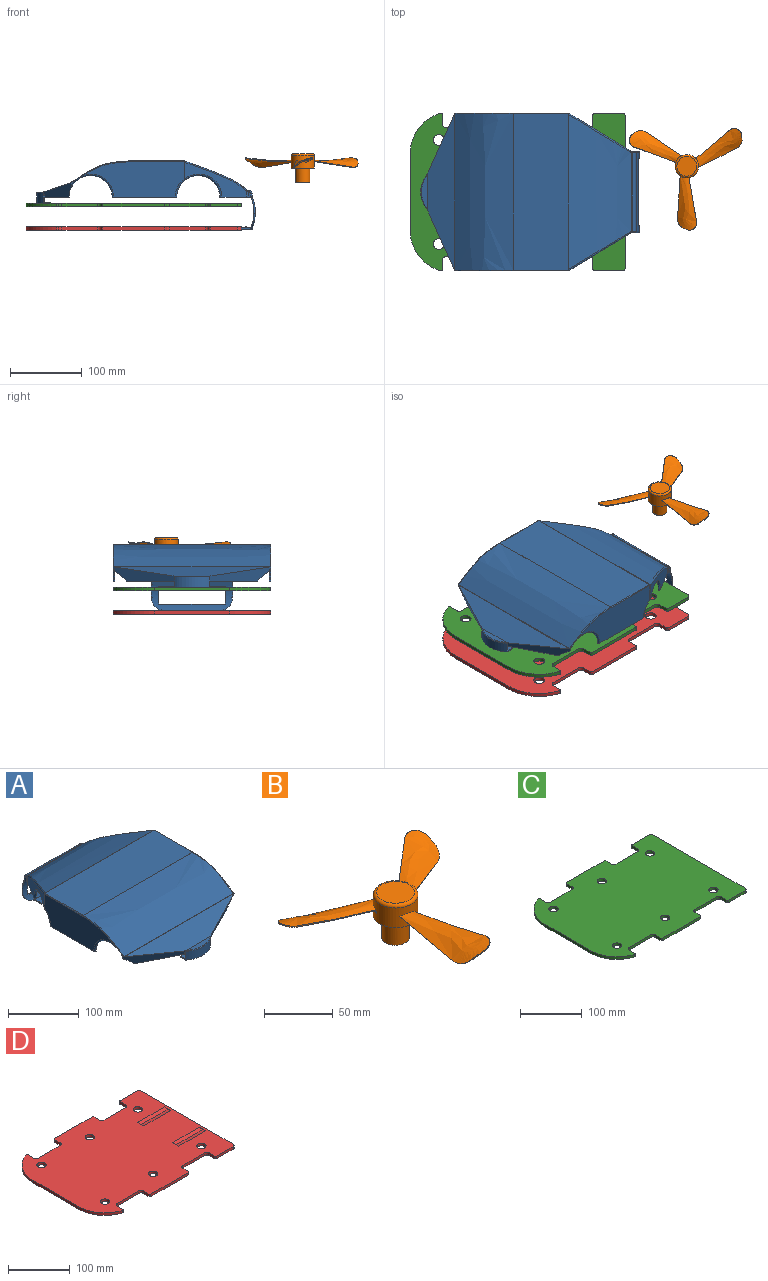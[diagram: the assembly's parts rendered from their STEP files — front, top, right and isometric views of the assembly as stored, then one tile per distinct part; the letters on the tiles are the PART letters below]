
ASSEMBLY  parts=4 mates=1
PART A: 142 faces, bbox 290.9x334.2x135.4 mm
  f0: plane 140.21x49.36mm, normal (-1,0,0), area 5203mm2, adj f11,f53,f54,f100,f103,f104,f107
  f1: plane 4.65x4.5mm, normal (1,0,0), area 5.3mm2, adj f18,f25,f92,f108
  f2: plane 69.31x35.81mm, normal (0,0,-1), area 196.7mm2, adj f10,f24,f26,f47,f49,f63
  f3: plane 69.31x35.81mm, normal (0,0,-1), area 196.7mm2, adj f10,f25,f27,f48,f50,f62
  f4: plane 7.65x3.42mm, normal (1,0,0), area 22.2mm2, adj f6,f8,f82,f131,f132,f133,f134
  f5: plane 7.65x3.42mm, normal (-1,0,0), area 22.2mm2, adj f6,f8,f83,f116,f117,f118,f119
  f6: cylinder r=51mm len=113mm, axis (1,0,0), area 2556.2mm2, adj f4,f5,f8,f56,f57,f58,f59,f60
  f7: cylinder r=51mm len=109.01mm, axis (1,0,0), area 2172.4mm2, adj f58,f59,f60,f61,f76,f84,f111,f112
  f8: plane 156.92x43.12mm, normal (0,0,-1), area 296.3mm2, adj f4,f5,f6,f28,f29,f30,f31,f32
  f9: cylinder r=30mm len=44.38mm, axis (1,0,0), area 38.2mm2, adj f11,f31,f35,f100,f101
  f10: cylinder r=30mm len=216mm, axis (1,0,0), area 2858.4mm2, adj f2,f3,f11,f20,f24,f25,f35,f36
  f11: plane 90x2.5mm, normal (0,0,-1), area 223.3mm2, adj f0,f9,f10,f35,f100,f107
  f12: plane 109x3.29mm, normal (0,1,0), area 358.1mm2, adj f84,f85,f117,f133
  f13: plane 109.15x1.32mm, normal (0,0,1), area 143.8mm2, adj f52,f85,f119,f120,f130,f131
  f14: extruded ~215.73x86.9mm, area 15564.6mm2, adj f52,f122,f123,f125,f127,f128
  f15: plane 140.2x49.35mm, normal (1,0,0), area 5203mm2, adj f20,f55,f86,f94,f96,f98,f108
  f16: plane 4.65x4.5mm, normal (-1,0,0), area 5.3mm2, adj f18,f24,f90,f107
  f17: cylinder r=30mm len=44.38mm, axis (1,0,0), area 38.2mm2, adj f20,f32,f36,f93,f94
  f18: plane 220x39.17mm, normal (0,-0.32,0.95), area 5384.8mm2, adj f1,f16,f19,f24,f25,f51,f90,f91
  f19: plane 46.85x8.19mm, normal (0,0,1), area 261.9mm2, adj f18,f51
  f20: plane 90x2.5mm, normal (0,0,-1), area 223.3mm2, adj f10,f15,f17,f36,f94,f108
  f21: plane 218x76.61mm, normal (0,0,1), area 16698.8mm2, adj f53,f86,f88,f99,f106,f125
  f22: extruded ~218x81.16mm, area 19256.8mm2, adj f54,f55,f88,f91
  f23: cylinder r=38.6mm len=50mm, axis (0,0,1), area 815.8mm2, adj f26,f27,f51,f62,f63,f65,f66,f68
  f24: plane 86.5x40.17mm, normal (-0.43,-0.86,-0.29), area 1148.9mm2, adj f2,f10,f16,f18,f26,f51,f107
  f25: plane 86.5x40.17mm, normal (0.43,-0.86,-0.29), area 1148.9mm2, adj f1,f3,f10,f18,f27,f51,f108
  f26: plane 6.55x2.41mm, normal (-1,0,0), area 8.2mm2, adj f2,f23,f24,f51
  f27: plane 6.55x2.41mm, normal (1,0,0), area 8.2mm2, adj f3,f23,f25,f51
  f28: plane 85.83x52.48mm, normal (0.85,0.52,0), area 1537mm2, adj f8,f82,f93,f96,f99,f127
  f29: plane 85.83x52.48mm, normal (-0.85,0.52,0), area 1537mm2, adj f8,f83,f101,f103,f106,f123
  f30: plane 6.86x4.89mm, normal (1,0,0), area 28.2mm2, adj f8,f31,f39,f81
  f31: plane 113.84x79.83mm, normal (0.85,-0.52,0), area 1661.3mm2, adj f8,f9,f30,f34,f35,f37,f38,f81
  f32: plane 113.84x79.83mm, normal (-0.85,-0.52,0), area 1661.3mm2, adj f8,f17,f33,f34,f36,f37,f38,f81
  f33: plane 6.86x4.89mm, normal (-1,0,0), area 28.2mm2, adj f8,f32,f39,f81
  f34: plane 215x76.48mm, normal (0,0,-1), area 16442.6mm2, adj f31,f32,f35,f36,f37,f40
  f35: plane 144.72x51.2mm, normal (1,0,0), area 5156.1mm2, adj f9,f10,f11,f31,f34,f40
  f36: plane 144.72x51.2mm, normal (-1,0,0), area 5156.1mm2, adj f10,f17,f20,f32,f34,f40
  f37: extruded ~214.67x87.02mm, area 16480mm2, adj f31,f32,f34,f38
  f38: plane 108.27x0.11mm, normal (0,0,-1), area 12mm2, adj f31,f32,f37,f81
  f39: plane 108x1.86mm, normal (0,-1,0), area 200.7mm2, adj f8,f30,f33,f81
  f40: extruded ~215x65.15mm, area 14889.9mm2, adj f10,f34,f35,f36
  f41: plane 4.43x4.18mm, normal (1,0,0), area 3.5mm2, adj f10,f45,f47
  f42: plane 4.43x4.18mm, normal (-1,0,0), area 3.5mm2, adj f10,f45,f48
  f43: plane 209.79x38.93mm, normal (0,0.32,-0.95), area 5068.9mm2, adj f44,f45,f46,f47,f48,f49,f50
  f44: plane 43x7.1mm, normal (0,0,-1), area 207.9mm2, adj f43,f46
  f45: extruded ~215x5.24mm, area 1358.9mm2, adj f10,f41,f42,f43,f47,f48
  f46: cylinder r=36.1mm len=45mm, axis (0,0,1), area 559mm2, adj f43,f44,f49,f50,f62,f63,f64
  f47: plane 85x38.64mm, normal (0.43,0.86,0.29), area 903.3mm2, adj f2,f10,f41,f43,f45,f49
  f48: plane 85x38.64mm, normal (-0.43,0.86,0.29), area 903.3mm2, adj f3,f10,f42,f43,f45,f50
  f49: plane 5.14x2.85mm, normal (1,0,0), area 10mm2, adj f2,f43,f46,f47
  f50: plane 5.14x2.85mm, normal (-1,0,0), area 10mm2, adj f3,f43,f46,f48
  f51: torus R=37.6mm, axis (0,0,1), area 82.6mm2, adj f18,f19,f23,f24,f25,f26,f27
  f52: cylinder r=1mm len=110.34mm, axis (-1,0,0), area 77.6mm2, adj f13,f14,f121,f129
  f53: cylinder r=1mm len=74.76mm, axis (0,-1,0), area 117.4mm2, adj f0,f21,f89,f104
  f54: bspline ~90.06x34.33mm, area 129.4mm2, adj f0,f22,f89,f90,f107
  f55: bspline ~92.12x34.46mm, area 129.4mm2, adj f15,f22,f87,f92,f108
  f56: cylinder r=20mm len=19.36mm, axis (0,1,0), area 8.6mm2, adj f6,f75,f112
  f57: cylinder r=20mm len=19.36mm, axis (0,1,0), area 8.6mm2, adj f6,f77,f138
  f58: plane 24.03x3.79mm, normal (1,0,0), area 48.1mm2, adj f6,f7,f59,f61
  f59: plane 93x2mm, normal (0,0,-1), area 186mm2, adj f6,f7,f58,f60
  f60: plane 24.03x3.79mm, normal (-1,0,0), area 48.1mm2, adj f6,f7,f59,f61
  f61: plane 93x2mm, normal (0,0,1), area 186mm2, adj f6,f7,f58,f60
  f62: plane 7x2.5mm, normal (0.43,0.9,0), area 19.4mm2, adj f3,f23,f46,f64
  f63: plane 7x2.5mm, normal (-0.43,0.9,0), area 19.4mm2, adj f2,f23,f46,f64
  f64: plane 50x16.69mm, normal (0,0,1), area 685.7mm2, adj f46,f62,f63,f65,f66,f67
  f65: plane 10x2mm, normal (1,0,0), area 20mm2, adj f23,f64,f67,f68
  f66: plane 10x2mm, normal (-1,0,0), area 20mm2, adj f23,f64,f67,f68
  f67: plane 50x2mm, normal (0,1,0), area 100mm2, adj f64,f65,f66,f68
  f68: plane 50x19.19mm, normal (0,0,-1), area 814.4mm2, adj f23,f65,f66,f67
  f69: plane 13x2mm, normal (1,0,0), area 25mm2, adj f6,f70,f73,f74
  f70: plane 73x2mm, normal (0,-1,0), area 146mm2, adj f69,f71,f73,f74
  f71: plane 13x2mm, normal (-1,0,0), area 25mm2, adj f6,f70,f73,f74
  f72: plane 69.45x0.93mm, normal (0,1,0), area 63.9mm2, adj f73,f76,f109,f141
  f73: plane 73.07x15.07mm, normal (0,0,-1), area 1093mm2, adj f69,f70,f71,f72,f75,f77,f109,f110
  f74: plane 73x13mm, normal (0,0,1), area 899mm2, adj f6,f69,f70,f71,f78,f79,f80
  f75: cylinder r=5mm len=3.4mm, axis (0,-1,0), area 3.5mm2, adj f6,f56,f73,f110,f111
  f76: cylinder r=5mm len=75.7mm, axis (1,0,0), area 149.8mm2, adj f7,f72,f110,f140
  f77: cylinder r=5mm len=3.4mm, axis (0,-1,0), area 3.5mm2, adj f6,f57,f73,f139,f140
  f78: plane 5x1.24mm, normal (1,0,0), area 4.3mm2, adj f74,f80
  f79: plane 5x1.24mm, normal (-1,0,0), area 4.3mm2, adj f74,f80
  f80: cylinder r=3.14mm len=10mm, axis (-1,0,0), area 57.8mm2, adj f74,f78,f79
  f81: cylinder r=5mm len=108.13mm, axis (-1,0,0), area 848.2mm2, adj f30,f31,f32,f33,f38,f39
  f82: cylinder r=5mm len=8.64mm, axis (0,0,-1), area 21.3mm2, adj f4,f8,f28,f128,f129,f130
  f83: cylinder r=5mm len=8.64mm, axis (0,0,-1), area 21.3mm2, adj f5,f8,f29,f120,f121,f122
  f84: cylinder r=5mm len=109.01mm, axis (1,0,0), area 225.1mm2, adj f7,f12,f115,f116,f134,f135
  f85: cylinder r=5mm len=109mm, axis (1,0,0), area 856.1mm2, adj f12,f13,f118,f132
  f86: cylinder r=1mm len=74.76mm, axis (0,1,0), area 117.4mm2, adj f15,f21,f87,f98
  f87: sphere r=1mm, area 0.1mm2, adj f55,f86,f88
  f88: cylinder r=1mm len=218mm, axis (-1,0,0), area 13.4mm2, adj f21,f22,f87,f89
  f89: sphere r=1mm, area 0.1mm2, adj f53,f54,f88
  f90: bspline ~9.24x4.77mm, area 3mm2, adj f16,f18,f54,f91,f107
  f91: cylinder r=2mm len=218mm, axis (-1,0,0), area 119.6mm2, adj f18,f22,f90,f92
  f92: bspline ~9.24x4.77mm, area 3mm2, adj f1,f18,f55,f91,f108
  f93: bspline ~51.76x33.35mm, area 257.2mm2, adj f8,f17,f28,f32,f95
  f94: torus R=32mm, axis (1,0,0), area 87.4mm2, adj f15,f17,f20,f95
  f95: sphere r=2mm, area 0.9mm2, adj f93,f94,f96
  f96: cylinder r=2mm len=23.69mm, axis (0,0,1), area 25.7mm2, adj f15,f28,f95,f97
  f97: bspline ~1.19x1.17mm, area 0.3mm2, adj f96,f98,f99
  f98: bspline ~2.08x1.48mm, area 2.4mm2, adj f15,f86,f97,f99
  f99: cylinder r=2mm len=2.9mm, axis (-0.52,0.85,0), area 3.6mm2, adj f21,f28,f97,f98,f126
  f100: torus R=32mm, axis (1,0,0), area 87.4mm2, adj f0,f9,f11,f102
  f101: bspline ~51.76x33.35mm, area 257.2mm2, adj f8,f9,f29,f31,f102
  f102: sphere r=2mm, area 0.9mm2, adj f100,f101,f103
  f103: cylinder r=2mm len=23.69mm, axis (0,0,1), area 25.7mm2, adj f0,f29,f102,f105
  f104: bspline ~2.08x1.48mm, area 2.4mm2, adj f0,f53,f105,f106
  f105: bspline ~1.19x1.17mm, area 0.3mm2, adj f103,f104,f106
  f106: cylinder r=2mm len=2.9mm, axis (-0.52,-0.85,0), area 3.6mm2, adj f21,f29,f104,f105,f124
  f107: torus R=32mm, axis (1,0,0), area 245.2mm2, adj f0,f10,f11,f16,f24,f54,f90
  f108: torus R=32mm, axis (1,0,0), area 245.2mm2, adj f1,f10,f15,f20,f25,f55,f92
  f109: torus R=7mm, axis (0,-1,0), area 1.1mm2, adj f72,f73,f110
  f110: bspline ~4.75x3.9mm, area 8.9mm2, adj f73,f75,f76,f109,f111
  f111: bspline ~3.65x2.44mm, area 3.6mm2, adj f7,f75,f110,f112
  f112: bspline ~20.17x18.08mm, area 75.6mm2, adj f7,f56,f111,f113
  f113: bspline ~2.33x2.06mm, area 1.1mm2, adj f6,f7,f112,f114
  f114: bspline ~28.6x7.75mm, area 68.6mm2, adj f6,f7,f113,f115
  f115: bspline ~2.33x2.02mm, area 3.7mm2, adj f6,f84,f114,f116
  f116: torus R=7mm, axis (1,0,0), area 3.5mm2, adj f5,f84,f115,f117
  f117: cylinder r=2mm len=3.29mm, axis (0,0,1), area 10.3mm2, adj f5,f12,f116,f118
  f118: torus R=3mm, axis (1,0,0), area 21.1mm2, adj f5,f85,f117,f119
  f119: cylinder r=2mm len=2mm, axis (0,-1,0), area 0.9mm2, adj f5,f13,f118,f120
  f120: torus R=7mm, axis (0,0,1), area 2.7mm2, adj f13,f83,f119,f121
  f121: bspline ~2.51x2.28mm, area 3mm2, adj f52,f83,f120,f122
  f122: bspline ~3.84x3.01mm, area 2.1mm2, adj f14,f83,f121,f123
  f123: bspline ~126.47x78.37mm, area 294.1mm2, adj f14,f29,f122,f124
  f124: sphere r=2mm, area 1.1mm2, adj f106,f123,f125
  f125: cylinder r=2mm len=215.73mm, axis (-1,0,0), area 147.2mm2, adj f14,f21,f124,f126
  f126: sphere r=2mm, area 1.1mm2, adj f99,f125,f127
  f127: bspline ~126.47x78.37mm, area 294.1mm2, adj f14,f28,f126,f128
  f128: bspline ~3.84x3.01mm, area 2.1mm2, adj f14,f82,f127,f129
  f129: bspline ~2.51x2.28mm, area 3mm2, adj f52,f82,f128,f130
  f130: torus R=7mm, axis (0,0,1), area 2.7mm2, adj f13,f82,f129,f131
  f131: cylinder r=2mm len=2mm, axis (0,1,0), area 0.9mm2, adj f4,f13,f130,f132
  f132: torus R=3mm, axis (1,0,0), area 21.1mm2, adj f4,f85,f131,f133
  f133: cylinder r=2mm len=3.29mm, axis (0,0,-1), area 10.3mm2, adj f4,f12,f132,f134
  f134: torus R=7mm, axis (1,0,0), area 3.5mm2, adj f4,f84,f133,f135
  f135: bspline ~2.33x2.02mm, area 3.7mm2, adj f6,f84,f134,f136
  f136: bspline ~28.6x7.75mm, area 68.6mm2, adj f6,f7,f135,f137
  f137: bspline ~2.33x2.06mm, area 1.1mm2, adj f6,f7,f136,f138
  f138: bspline ~21.03x18.87mm, area 75.6mm2, adj f7,f57,f137,f139
  f139: bspline ~4.48x2.46mm, area 3.6mm2, adj f7,f77,f138,f140
  f140: bspline ~5.44x4.12mm, area 8.9mm2, adj f73,f76,f77,f139,f141
  f141: torus R=7mm, axis (0,-1,0), area 1.1mm2, adj f72,f73,f140
PART B: 59 faces, bbox 180.5x163.3x41 mm
  f0: plane 9.5x6.92mm, normal (0,0,-1), area 30mm2, adj f6,f23,f47,f57
  f1: cylinder r=13.12mm len=15mm, axis (0,0,-1), area 168.6mm2, adj f2,f13,f55,f58
  f2: plane 10.9x3.96mm, normal (0,0,-1), area 30mm2, adj f1,f6,f55,f58
  f3: cylinder r=13.12mm len=15mm, axis (0,0,-1), area 168.6mm2, adj f4,f13,f53,f56
  f4: plane 9.38x7.12mm, normal (0,0,-1), area 30mm2, adj f3,f6,f53,f56
  f5: cylinder r=13.12mm len=18.4mm, axis (0,0,-1), area 348.6mm2, adj f7,f13,f48,f50,f51,f52,f54
  f6: cylinder r=10mm len=35mm, axis (0,0,-1), area 1983.9mm2, adj f0,f2,f4,f7,f9,f13,f25,f46
  f7: plane 18.4x12.02mm, normal (0,0,-1), area 67.8mm2, adj f5,f6,f48,f54
  f8: cylinder r=13.12mm len=15mm, axis (0,0,-1), area 168.6mm2, adj f9,f13,f46,f49
  f9: plane 9.38x7.12mm, normal (0,0,-1), area 30mm2, adj f6,f8,f46,f49
  f10: plane 15x13.75mm, normal (0,0,-1), area 169.7mm2, adj f24,f26
  f11: cylinder r=16.25mm len=32.5mm, axis (0,0,-1), area 1741.4mm2, adj f13,f14,f16,f17,f18,f22,f29,f30
  f12: plane 27.5x27.5mm, normal (0,0,1), area 594mm2, adj f14
  f13: plane 32.5x32.5mm, normal (0,0,-1), area 335.4mm2, adj f1,f3,f5,f6,f8,f11,f23,f46
  f14: torus R=13.75mm, axis (0,0,1), area 378.5mm2, adj f11,f12
  f15: bspline ~58.99x10.6mm, area 59.9mm2, adj f17,f18,f19,f22
  f16: bspline ~70.83x11.04mm, area 58mm2, adj f11,f17,f18,f21
  f17: offset ~76.3x29.48mm, area 1505.3mm2, adj f11,f15,f16,f19,f20,f21,f22,f27
  f18: offset ~101x33.5mm, area 1565.4mm2, adj f11,f15,f16,f19,f20,f21,f22,f27
  f19: bspline ~14.93x11.81mm, area 23mm2, adj f15,f17,f18,f20
  f20: bspline ~6.21x4.45mm, area 7.3mm2, adj f17,f18,f19,f27
  f21: bspline ~9.82x2.06mm, area 0.7mm2, adj f16,f17,f18,f27
  f22: bspline ~3.02x2.64mm, area 3.7mm2, adj f11,f15,f17,f18
  f23: cylinder r=13.12mm len=15mm, axis (0,0,-1), area 168.6mm2, adj f0,f13,f47,f57
  f24: cylinder r=7.5mm len=35mm, axis (0,0,-1), area 1341.9mm2, adj f10,f25,f26
  f25: plane 20x20mm, normal (0,0,-1), area 144.5mm2, adj f6,f24,f26
  f26: plane 35x8.29mm, normal (0,-1,0), area 290.2mm2, adj f10,f24,f25
  f27: bspline ~13.5x9.07mm, area 16.6mm2, adj f17,f18,f20,f21
  f28: bspline ~56.33x20.66mm, area 59.9mm2, adj f30,f31,f32,f35
  f29: bspline ~48.25x32.17mm, area 58mm2, adj f11,f30,f31,f34
  f30: offset ~78.23x56.09mm, area 1505.3mm2, adj f11,f28,f29,f32,f33,f34,f35,f36
  f31: offset ~100.9x68.02mm, area 1565.4mm2, adj f11,f28,f29,f32,f33,f34,f35,f36
  f32: bspline ~18.07x6.72mm, area 23mm2, adj f28,f30,f31,f33
  f33: bspline ~9.94x8.28mm, area 7.3mm2, adj f30,f31,f32,f36
  f34: bspline ~8.51x6.07mm, area 0.7mm2, adj f29,f30,f31,f36
  f35: bspline ~3.4x2.64mm, area 3.7mm2, adj f11,f28,f30,f31
  f36: bspline ~15.19x9.07mm, area 16.6mm2, adj f30,f31,f33,f34
  f37: bspline ~45.99x38.64mm, area 59.9mm2, adj f39,f40,f41,f44
  f38: bspline ~63.66x32.1mm, area 58mm2, adj f11,f39,f40,f43
  f39: offset ~76.28x59.47mm, area 1505.3mm2, adj f11,f37,f38,f41,f42,f43,f44,f45
  f40: offset ~76.56x59.62mm, area 1565.4mm2, adj f11,f37,f38,f41,f42,f43,f44,f45
  f41: bspline ~16.58x9.86mm, area 23mm2, adj f37,f39,f40,f42
  f42: bspline ~6.85x4.45mm, area 7.3mm2, adj f39,f40,f41,f45
  f43: bspline ~9.17x5.02mm, area 0.7mm2, adj f38,f39,f40,f45
  f44: bspline ~3.7x2.64mm, area 3.7mm2, adj f11,f37,f39,f40
  f45: bspline ~12.85x10.17mm, area 16.6mm2, adj f39,f40,f42,f43
  f46: plane 15x3.15mm, normal (0,-1,0), area 47.2mm2, adj f6,f8,f9,f13
  f47: plane 15x3.14mm, normal (0,1,0), area 47.1mm2, adj f0,f6,f13,f23
  f48: plane 15x2.73mm, normal (-0.87,-0.5,0), area 47.2mm2, adj f5,f6,f7,f13
  f49: plane 15x2.72mm, normal (0.87,0.5,0), area 47.1mm2, adj f6,f8,f9,f13
  f50: bspline ~100x16.99mm, area 8mm2, adj f5,f6,f51,f52
  f51: plane 10.82x2.74mm, normal (0.87,-0.5,0), area 33.6mm2, adj f5,f6,f13,f50
  f52: plane 10.88x2.74mm, normal (-0.87,0.5,0), area 33.4mm2, adj f5,f6,f13,f50
  f53: plane 15x3.15mm, normal (0,1,0), area 47.2mm2, adj f3,f4,f6,f13
  f54: plane 15x3.14mm, normal (0,-1,0), area 47.1mm2, adj f5,f6,f7,f13
  f55: plane 15x2.73mm, normal (0.87,0.5,0), area 47.2mm2, adj f1,f2,f6,f13
  f56: plane 15x2.72mm, normal (-0.87,-0.5,0), area 47.1mm2, adj f3,f4,f6,f13
  f57: plane 15x2.73mm, normal (0.87,-0.5,0), area 47.2mm2, adj f0,f6,f13,f23
  f58: plane 15x2.72mm, normal (-0.87,0.5,0), area 47.1mm2, adj f1,f2,f6,f13
PART C: 54 faces, bbox 300x220x5 mm
  f0: plane 300x220mm, normal (0,0,-1), area 57151mm2, adj f2,f3,f4,f5,f6,f7,f8,f9
  f1: plane 300x220mm, normal (0,0,1), area 58859mm2, adj f2,f3,f4,f5,f6,f7,f8,f9
  f2: plane 86x5mm, normal (0,1,0), area 430mm2, adj f0,f1,f36,f42
  f3: plane 86x5mm, normal (0,-1,0), area 430mm2, adj f0,f1,f38,f41
  f4: plane 38x5mm, normal (0,-1,0), area 190mm2, adj f0,f1,f34,f40
  f5: plane 210x5mm, normal (1,0,0), area 1050mm2, adj f0,f1,f34,f35
  f6: plane 104.92x5mm, normal (-1,0,0), area 524.6mm2, adj f0,f1,f44,f45
  f7: plane 38x5mm, normal (0,1,0), area 190mm2, adj f0,f1,f35,f37
  f8: cylinder r=5mm len=5mm, axis (0,0,1), area 39.3mm2, adj f0,f1,f9,f11
  f9: plane 50x5mm, normal (0,-1,0), area 250mm2, adj f0,f1,f8,f10
  f10: cylinder r=5mm len=5mm, axis (0,0,1), area 39.3mm2, adj f0,f1,f9,f12
  f11: plane 13x5mm, normal (-1,0,0), area 65mm2, adj f0,f1,f8,f40
  f12: plane 13x5mm, normal (1,0,0), area 65mm2, adj f0,f1,f10,f41
  f13: cylinder r=5mm len=5mm, axis (0,0,1), area 39.3mm2, adj f0,f1,f14,f16
  f14: plane 50x5mm, normal (0,-1,0), area 250mm2, adj f0,f1,f13,f15
  f15: cylinder r=5mm len=5mm, axis (0,0,1), area 39.3mm2, adj f0,f1,f14,f17
  f16: plane 13x5mm, normal (-1,0,0), area 65mm2, adj f0,f1,f13,f38
  f17: plane 13x5mm, normal (1,0,0), area 65mm2, adj f0,f1,f15,f39
  f18: cylinder r=5mm len=5mm, axis (0,0,1), area 39.3mm2, adj f0,f1,f19,f21
  f19: plane 50x5mm, normal (0,1,0), area 250mm2, adj f0,f1,f18,f20
  f20: cylinder r=5mm len=5mm, axis (0,0,1), area 39.3mm2, adj f0,f1,f19,f22
  f21: plane 13x5mm, normal (1,0,0), area 65mm2, adj f0,f1,f18,f36
  f22: plane 13x5mm, normal (-1,0,0), area 65mm2, adj f0,f1,f20,f37
  f23: plane 13x5mm, normal (1,0,0), area 65mm2, adj f0,f1,f24,f43
  f24: cylinder r=5mm len=5mm, axis (0,0,1), area 39.3mm2, adj f0,f1,f23,f25
  f25: plane 50x5mm, normal (0,1,0), area 250mm2, adj f0,f1,f24,f26
  f26: cylinder r=5mm len=5mm, axis (0,0,1), area 39.3mm2, adj f0,f1,f25,f27
  f27: plane 13x5mm, normal (-1,0,0), area 65mm2, adj f0,f1,f26,f42
  f28: cylinder r=7.5mm len=15mm, axis (0,0,1), area 235.6mm2, adj f0,f1
  f29: cylinder r=7.5mm len=15mm, axis (0,0,1), area 235.6mm2, adj f0,f1
  f30: cylinder r=7.5mm len=15mm, axis (0,0,1), area 235.6mm2, adj f0,f1
  f31: cylinder r=7.5mm len=15mm, axis (0,0,1), area 235.6mm2, adj f0,f1
  f32: cylinder r=7.5mm len=15mm, axis (0,0,1), area 235.6mm2, adj f0,f1
  f33: cylinder r=7.5mm len=15mm, axis (0,0,1), area 235.6mm2, adj f0,f1
  f34: cylinder r=5mm len=5mm, axis (0,0,1), area 39.3mm2, adj f0,f1,f4,f5
  f35: cylinder r=5mm len=5mm, axis (0,0,-1), area 39.3mm2, adj f0,f1,f5,f7
  f36: cylinder r=2mm len=5mm, axis (0,0,-1), area 15.7mm2, adj f0,f1,f2,f21
  f37: cylinder r=2mm len=5mm, axis (0,0,1), area 15.7mm2, adj f0,f1,f7,f22
  f38: cylinder r=2mm len=5mm, axis (0,0,-1), area 15.7mm2, adj f0,f1,f3,f16
  f39: cylinder r=2mm len=5mm, axis (0,0,1), area 15.7mm2, adj f0,f1,f17,f44
  f40: cylinder r=2mm len=5mm, axis (0,0,-1), area 15.7mm2, adj f0,f1,f4,f11
  f41: cylinder r=2mm len=5mm, axis (0,0,1), area 15.7mm2, adj f0,f1,f3,f12
  f42: cylinder r=2mm len=5mm, axis (0,0,1), area 15.7mm2, adj f0,f1,f2,f27
  f43: cylinder r=2mm len=5mm, axis (0,0,-1), area 15.7mm2, adj f0,f1,f23,f45
  f44: cylinder r=60mm len=57.54mm, axis (0,0,-1), area 385.1mm2, adj f0,f1,f6,f39
  f45: cylinder r=60mm len=57.54mm, axis (0,0,1), area 385.1mm2, adj f0,f1,f6,f43
  f46: plane 14x1.38mm, normal (1,0,0), area 11.5mm2, adj f0,f48,f49
  f47: plane 14x1.38mm, normal (-1,0,0), area 11.5mm2, adj f0,f48,f49
  f48: cylinder r=33mm len=61mm, axis (1,0,0), area 436mm2, adj f0,f46,f47,f49
  f49: cylinder r=33mm len=61mm, axis (1,0,0), area 436mm2, adj f0,f46,f47,f48
  f50: plane 14x1.38mm, normal (1,0,0), area 11.5mm2, adj f0,f52,f53
  f51: plane 14x1.38mm, normal (-1,0,0), area 11.5mm2, adj f0,f52,f53
  f52: cylinder r=33mm len=61mm, axis (1,0,0), area 436mm2, adj f0,f50,f51,f53
  f53: cylinder r=33mm len=61mm, axis (1,0,0), area 436mm2, adj f0,f50,f51,f52
PART D: 54 faces, bbox 300x220x5 mm
  f0: plane 300x220mm, normal (0,0,1), area 57151mm2, adj f2,f3,f4,f5,f6,f7,f8,f9
  f1: plane 300x220mm, normal (0,0,-1), area 58859mm2, adj f2,f3,f4,f5,f6,f7,f8,f9
  f2: plane 86x5mm, normal (0,1,0), area 430mm2, adj f0,f1,f36,f42
  f3: plane 86x5mm, normal (0,-1,0), area 430mm2, adj f0,f1,f38,f41
  f4: plane 38x5mm, normal (0,-1,0), area 190mm2, adj f0,f1,f34,f40
  f5: plane 210x5mm, normal (1,0,0), area 1050mm2, adj f0,f1,f34,f35
  f6: plane 104.92x5mm, normal (-1,0,0), area 524.6mm2, adj f0,f1,f44,f45
  f7: plane 38x5mm, normal (0,1,0), area 190mm2, adj f0,f1,f35,f37
  f8: cylinder r=5mm len=5mm, axis (0,0,-1), area 39.3mm2, adj f0,f1,f9,f11
  f9: plane 50x5mm, normal (0,-1,0), area 250mm2, adj f0,f1,f8,f10
  f10: cylinder r=5mm len=5mm, axis (0,0,-1), area 39.3mm2, adj f0,f1,f9,f12
  f11: plane 13x5mm, normal (-1,0,0), area 65mm2, adj f0,f1,f8,f40
  f12: plane 13x5mm, normal (1,0,0), area 65mm2, adj f0,f1,f10,f41
  f13: cylinder r=5mm len=5mm, axis (0,0,-1), area 39.3mm2, adj f0,f1,f14,f16
  f14: plane 50x5mm, normal (0,-1,0), area 250mm2, adj f0,f1,f13,f15
  f15: cylinder r=5mm len=5mm, axis (0,0,-1), area 39.3mm2, adj f0,f1,f14,f17
  f16: plane 13x5mm, normal (-1,0,0), area 65mm2, adj f0,f1,f13,f38
  f17: plane 13x5mm, normal (1,0,0), area 65mm2, adj f0,f1,f15,f39
  f18: cylinder r=5mm len=5mm, axis (0,0,-1), area 39.3mm2, adj f0,f1,f19,f21
  f19: plane 50x5mm, normal (0,1,0), area 250mm2, adj f0,f1,f18,f20
  f20: cylinder r=5mm len=5mm, axis (0,0,-1), area 39.3mm2, adj f0,f1,f19,f22
  f21: plane 13x5mm, normal (1,0,0), area 65mm2, adj f0,f1,f18,f36
  f22: plane 13x5mm, normal (-1,0,0), area 65mm2, adj f0,f1,f20,f37
  f23: plane 13x5mm, normal (1,0,0), area 65mm2, adj f0,f1,f24,f43
  f24: cylinder r=5mm len=5mm, axis (0,0,-1), area 39.3mm2, adj f0,f1,f23,f25
  f25: plane 50x5mm, normal (0,1,0), area 250mm2, adj f0,f1,f24,f26
  f26: cylinder r=5mm len=5mm, axis (0,0,-1), area 39.3mm2, adj f0,f1,f25,f27
  f27: plane 13x5mm, normal (-1,0,0), area 65mm2, adj f0,f1,f26,f42
  f28: cylinder r=7.5mm len=15mm, axis (0,0,-1), area 235.6mm2, adj f0,f1
  f29: cylinder r=7.5mm len=15mm, axis (0,0,-1), area 235.6mm2, adj f0,f1
  f30: cylinder r=7.5mm len=15mm, axis (0,0,-1), area 235.6mm2, adj f0,f1
  f31: cylinder r=7.5mm len=15mm, axis (0,0,-1), area 235.6mm2, adj f0,f1
  f32: cylinder r=7.5mm len=15mm, axis (0,0,-1), area 235.6mm2, adj f0,f1
  f33: cylinder r=7.5mm len=15mm, axis (0,0,-1), area 235.6mm2, adj f0,f1
  f34: cylinder r=5mm len=5mm, axis (0,0,-1), area 39.3mm2, adj f0,f1,f4,f5
  f35: cylinder r=5mm len=5mm, axis (0,0,1), area 39.3mm2, adj f0,f1,f5,f7
  f36: cylinder r=2mm len=5mm, axis (0,0,1), area 15.7mm2, adj f0,f1,f2,f21
  f37: cylinder r=2mm len=5mm, axis (0,0,-1), area 15.7mm2, adj f0,f1,f7,f22
  f38: cylinder r=2mm len=5mm, axis (0,0,1), area 15.7mm2, adj f0,f1,f3,f16
  f39: cylinder r=2mm len=5mm, axis (0,0,-1), area 15.7mm2, adj f0,f1,f17,f44
  f40: cylinder r=2mm len=5mm, axis (0,0,1), area 15.7mm2, adj f0,f1,f4,f11
  f41: cylinder r=2mm len=5mm, axis (0,0,-1), area 15.7mm2, adj f0,f1,f3,f12
  f42: cylinder r=2mm len=5mm, axis (0,0,-1), area 15.7mm2, adj f0,f1,f2,f27
  f43: cylinder r=2mm len=5mm, axis (0,0,1), area 15.7mm2, adj f0,f1,f23,f45
  f44: cylinder r=60mm len=57.54mm, axis (0,0,1), area 385.1mm2, adj f0,f1,f6,f39
  f45: cylinder r=60mm len=57.54mm, axis (0,0,-1), area 385.1mm2, adj f0,f1,f6,f43
  f46: plane 14x1.38mm, normal (1,0,0), area 11.5mm2, adj f0,f48,f49
  f47: plane 14x1.38mm, normal (-1,0,0), area 11.5mm2, adj f0,f48,f49
  f48: cylinder r=33mm len=61mm, axis (1,0,0), area 436mm2, adj f0,f46,f47,f49
  f49: cylinder r=33mm len=61mm, axis (1,0,0), area 436mm2, adj f0,f46,f47,f48
  f50: plane 14x1.38mm, normal (1,0,0), area 11.5mm2, adj f0,f52,f53
  f51: plane 14x1.38mm, normal (-1,0,0), area 11.5mm2, adj f0,f52,f53
  f52: cylinder r=33mm len=61mm, axis (1,0,0), area 436mm2, adj f0,f50,f51,f53
  f53: cylinder r=33mm len=61mm, axis (1,0,0), area 436mm2, adj f0,f50,f51,f52
PLACE A rot(axis=(0,0,-1),90deg) t=(-16.43,43.32,152.28)mm
PLACE B t=(204.33,79.04,172.62)mm
PLACE C t=(-31.43,43.32,111.33)mm
PLACE D t=(-31.43,43.32,111.33)mm
MATE fastened A.f70 <-> D.f5  axis (-1,0,0) through (118.57,43.32,78.48)mm
